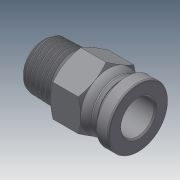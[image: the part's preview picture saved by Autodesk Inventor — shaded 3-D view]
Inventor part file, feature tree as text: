
AUTODESK INVENTOR PART (.ipt)
format: ipt  version: 2020.3 (Build 243373000, 373)  size: 724,992 bytes
history: native  units: in
note: dims shown in document units (in); Inventor stores cm internally (conversion verified against a paired STEP export)
features: revolve x3, fillet x1, other x1
ambient origin geometry x8: Origin, YZ Plane, XZ Plane, XY Plane, X Axis, Y Axis, Z Axis, Center Point
bodies: Solid1 (feature_tree), Solid2 (feature_tree), Solid3 (feature_tree), Solid4 (feature_tree), Solid5 (feature_tree)
feature tree (5):
  fillet  "Fillet1"  [1 undecoded]
  other  "Cut-Revolve3"
  revolve  "Revolve3"  [1 undecoded]
  revolve  "Revolve4"  [1 undecoded]
  revolve  "Revolve5"  [1 undecoded]
note: 4 required parameter values undecoded (feature->parameter linkage not recoverable at this tier; creation-order binding heuristic only, values carry confidence <= 0.55)
